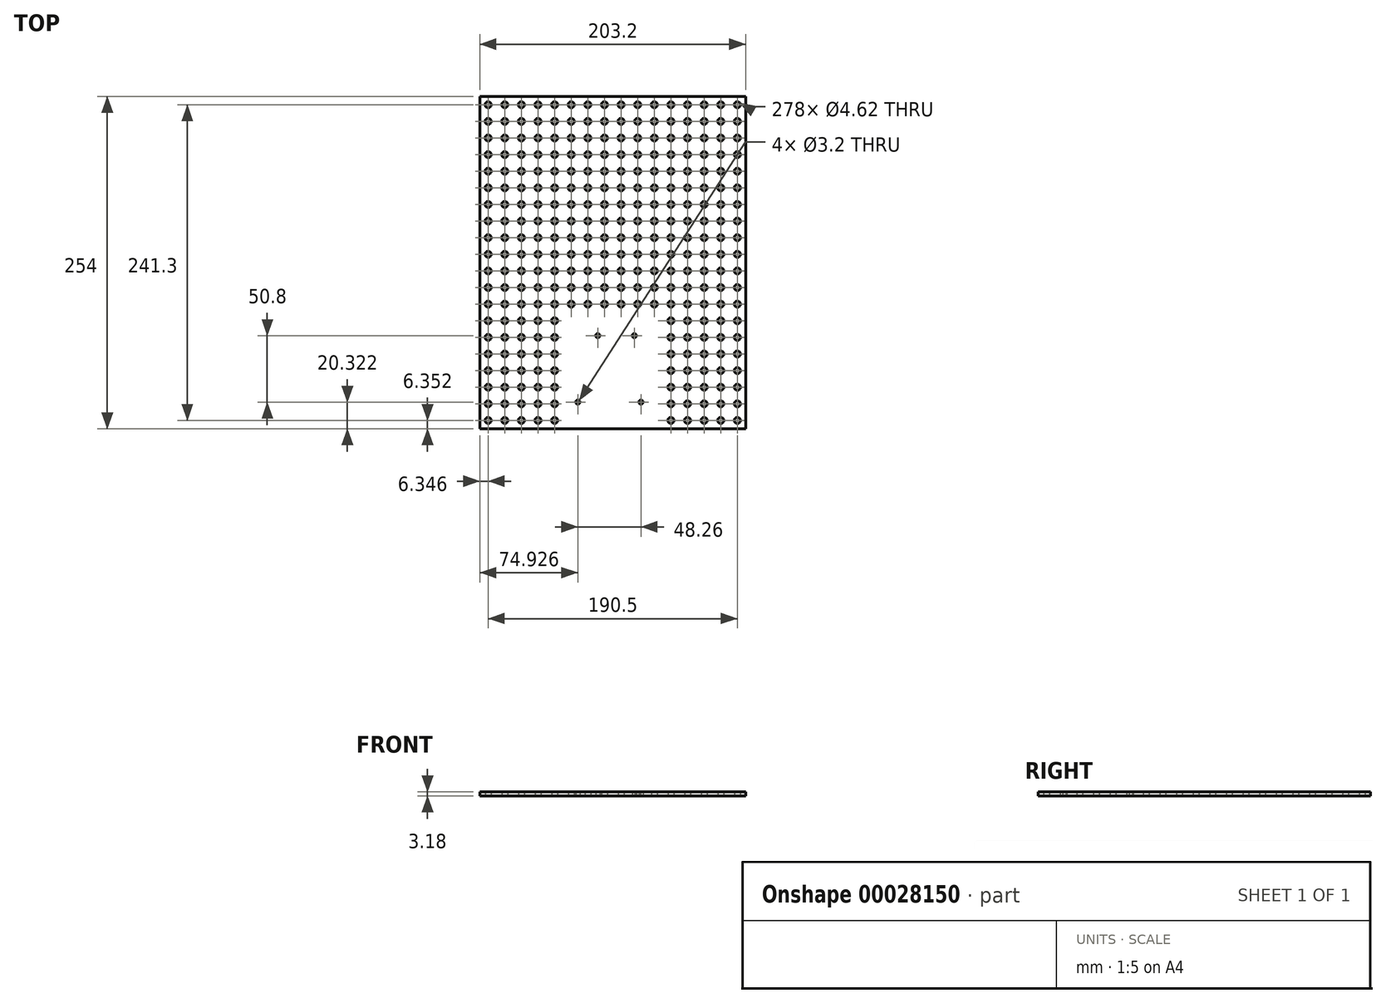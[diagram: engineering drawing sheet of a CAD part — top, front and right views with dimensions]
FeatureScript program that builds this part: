
annotation { "Feature Type Name" : "Feature", "Feature Type Description" : "" }
export const myFeature = defineFeature(function(context is Context, id is Id, definition is map)
    precondition{}
    {
        {
            var Q0;
            Q0=qCreatedBy(makeId("Top.planeOp"),FACE);
            var sketch = newSketch(context, id + "F0", { "sketchPlane" : qUnion([Q0])});
            skLineSegment(sketch, "E0.top", {"start": v(-127.4, -89.65) * mm, "end": v(-25.8, -89.65) * mm});
            skLineSegment(sketch, "E0.left", {"start": v(-127.4, 37.35) * mm, "end": v(-127.4, -89.65) * mm});
            skCircle(sketch, "E1", {"center": v(-121.04, 31) * mm, "radius": 2.31 * mm});
            skCircle(sketch, "E2", {"center": v(-121.04, 18.3) * mm, "radius": 2.31 * mm});
            skCircle(sketch, "E3", {"center": v(-121.04, 5.6) * mm, "radius": 2.31 * mm});
            skCircle(sketch, "E4", {"center": v(-121.04, -7.1) * mm, "radius": 2.31 * mm});
            skCircle(sketch, "E5", {"center": v(-121.04, -19.8) * mm, "radius": 2.31 * mm});
            skCircle(sketch, "E6", {"center": v(-121.04, -32.5) * mm, "radius": 2.31 * mm});
            skCircle(sketch, "E7", {"center": v(-121.04, -45.2) * mm, "radius": 2.31 * mm});
            skCircle(sketch, "E8", {"center": v(-121.04, -57.9) * mm, "radius": 2.31 * mm});
            skCircle(sketch, "E9", {"center": v(-121.04, -70.6) * mm, "radius": 2.31 * mm});
            skCircle(sketch, "E10", {"center": v(-121.04, -83.3) * mm, "radius": 2.31 * mm});
            skCircle(sketch, "E11.MirrorC", {"center": v(-108.34, 18.3) * mm, "radius": 2.31 * mm});
            skCircle(sketch, "E12.MirrorC", {"center": v(-108.34, -32.5) * mm, "radius": 2.31 * mm});
            skCircle(sketch, "E13.MirrorC", {"center": v(-108.34, -83.3) * mm, "radius": 2.31 * mm});
            skCircle(sketch, "E14.MirrorC", {"center": v(-108.34, -70.6) * mm, "radius": 2.31 * mm});
            skCircle(sketch, "E15.MirrorC", {"center": v(-108.34, 5.6) * mm, "radius": 2.31 * mm});
            skCircle(sketch, "E16.MirrorC", {"center": v(-108.34, -7.1) * mm, "radius": 2.31 * mm});
            skCircle(sketch, "E17.MirrorC", {"center": v(-108.34, -45.2) * mm, "radius": 2.31 * mm});
            skCircle(sketch, "E18.MirrorC", {"center": v(-108.34, -57.9) * mm, "radius": 2.31 * mm});
            skCircle(sketch, "E19.MirrorC", {"center": v(-108.34, -19.8) * mm, "radius": 2.31 * mm});
            skCircle(sketch, "E20.MirrorC", {"center": v(-108.34, 31) * mm, "radius": 2.31 * mm});
            skCircle(sketch, "E21.MirrorC", {"center": v(-95.64, -32.5) * mm, "radius": 2.31 * mm});
            skCircle(sketch, "E22.MirrorC", {"center": v(-82.94, -19.8) * mm, "radius": 2.31 * mm});
            skCircle(sketch, "E23.MirrorC", {"center": v(-95.64, 31) * mm, "radius": 2.31 * mm});
            skCircle(sketch, "E24.MirrorC", {"center": v(-95.64, -83.3) * mm, "radius": 2.31 * mm});
            skCircle(sketch, "E25.MirrorC", {"center": v(-82.94, -32.5) * mm, "radius": 2.31 * mm});
            skCircle(sketch, "E26.MirrorC", {"center": v(-95.64, 5.6) * mm, "radius": 2.31 * mm});
            skCircle(sketch, "E27.MirrorC", {"center": v(-95.64, -70.6) * mm, "radius": 2.31 * mm});
            skCircle(sketch, "E28.MirrorC", {"center": v(-82.94, -45.2) * mm, "radius": 2.31 * mm});
            skCircle(sketch, "E29.MirrorC", {"center": v(-95.64, -7.1) * mm, "radius": 2.31 * mm});
            skCircle(sketch, "E30.MirrorC", {"center": v(-82.94, -57.9) * mm, "radius": 2.31 * mm});
            skCircle(sketch, "E31.MirrorC", {"center": v(-95.64, -45.2) * mm, "radius": 2.31 * mm});
            skCircle(sketch, "E32.MirrorC", {"center": v(-95.64, -19.8) * mm, "radius": 2.31 * mm});
            skCircle(sketch, "E33.MirrorC", {"center": v(-82.94, 31) * mm, "radius": 2.31 * mm});
            skCircle(sketch, "E34.MirrorC", {"center": v(-82.94, 5.6) * mm, "radius": 2.31 * mm});
            skCircle(sketch, "E35.MirrorC", {"center": v(-95.64, 18.3) * mm, "radius": 2.31 * mm});
            skCircle(sketch, "E36.MirrorC", {"center": v(-82.94, -83.3) * mm, "radius": 2.31 * mm});
            skCircle(sketch, "E37.MirrorC", {"center": v(-95.64, -57.9) * mm, "radius": 2.31 * mm});
            skCircle(sketch, "E38.MirrorC", {"center": v(-82.94, 18.3) * mm, "radius": 2.31 * mm});
            skCircle(sketch, "E39.MirrorC", {"center": v(-82.94, -70.6) * mm, "radius": 2.31 * mm});
            skCircle(sketch, "E40.MirrorC", {"center": v(-82.94, -7.1) * mm, "radius": 2.31 * mm});
            skCircle(sketch, "E41.MirrorC", {"center": v(-70.24, -19.8) * mm, "radius": 2.31 * mm});
            skCircle(sketch, "E42.MirrorC", {"center": v(-70.24, -7.1) * mm, "radius": 2.31 * mm});
            skCircle(sketch, "E43.MirrorC", {"center": v(-44.84, 31) * mm, "radius": 2.31 * mm});
            skCircle(sketch, "E44.MirrorC", {"center": v(-70.24, 31) * mm, "radius": 2.31 * mm});
            skCircle(sketch, "E45.MirrorC", {"center": v(-57.54, 31) * mm, "radius": 2.31 * mm});
            skCircle(sketch, "E46.MirrorC", {"center": v(-44.84, 5.6) * mm, "radius": 2.31 * mm});
            skCircle(sketch, "E47.MirrorC", {"center": v(-70.24, -45.2) * mm, "radius": 2.31 * mm});
            skCircle(sketch, "E48.MirrorC", {"center": v(-70.24, 18.3) * mm, "radius": 2.31 * mm});
            skCircle(sketch, "E49.MirrorC", {"center": v(-70.24, 5.6) * mm, "radius": 2.31 * mm});
            skCircle(sketch, "E50.MirrorC", {"center": v(-70.24, -57.9) * mm, "radius": 2.31 * mm});
            skCircle(sketch, "E51.MirrorC", {"center": v(-57.54, 18.3) * mm, "radius": 2.31 * mm});
            skCircle(sketch, "E52.MirrorC", {"center": v(-32.14, 31) * mm, "radius": 2.31 * mm});
            skCircle(sketch, "E53.MirrorC", {"center": v(-70.24, -32.5) * mm, "radius": 2.31 * mm});
            skCircle(sketch, "E54.MirrorC", {"center": v(-32.14, 18.3) * mm, "radius": 2.31 * mm});
            skCircle(sketch, "E55.MirrorC", {"center": v(-44.84, 18.3) * mm, "radius": 2.31 * mm});
            skCircle(sketch, "E56.MirrorC", {"center": v(-57.54, 5.6) * mm, "radius": 2.31 * mm});
            skCircle(sketch, "E57.MirrorC", {"center": v(-70.24, -83.3) * mm, "radius": 2.31 * mm});
            skCircle(sketch, "E58.MirrorC", {"center": v(-32.14, 5.6) * mm, "radius": 2.31 * mm});
            skCircle(sketch, "E59.MirrorC", {"center": v(-70.24, -70.6) * mm, "radius": 2.31 * mm});
            skCircle(sketch, "E60.MirrorC", {"center": v(56.76, -7.1) * mm, "radius": 2.31 * mm});
            skCircle(sketch, "E61.MirrorC", {"center": v(44.06, -7.1) * mm, "radius": 2.31 * mm});
            skCircle(sketch, "E62.MirrorC", {"center": v(-19.44, 18.3) * mm, "radius": 2.31 * mm});
            skCircle(sketch, "E63.MirrorC", {"center": v(56.76, -83.3) * mm, "radius": 2.31 * mm});
            skCircle(sketch, "E64.MirrorC", {"center": v(44.06, 18.3) * mm, "radius": 2.31 * mm});
            skCircle(sketch, "E65.MirrorC", {"center": v(56.76, 5.6) * mm, "radius": 2.31 * mm});
            skCircle(sketch, "E66.MirrorC", {"center": v(56.76, 18.3) * mm, "radius": 2.31 * mm});
            skCircle(sketch, "E67.MirrorC", {"center": v(-19.44, 5.6) * mm, "radius": 2.31 * mm});
            skCircle(sketch, "E68.MirrorC", {"center": v(44.06, 5.6) * mm, "radius": 2.31 * mm});
            skCircle(sketch, "E69.MirrorC", {"center": v(18.66, -7.1) * mm, "radius": 2.31 * mm});
            skCircle(sketch, "E70.MirrorC", {"center": v(31.36, -19.8) * mm, "radius": 2.31 * mm});
            skCircle(sketch, "E71.MirrorC", {"center": v(69.46, -7.1) * mm, "radius": 2.31 * mm});
            skCircle(sketch, "E72.MirrorC", {"center": v(44.06, -32.5) * mm, "radius": 2.31 * mm});
            skCircle(sketch, "E73.MirrorC", {"center": v(44.06, -19.8) * mm, "radius": 2.31 * mm});
            skCircle(sketch, "E74.MirrorC", {"center": v(31.36, -70.6) * mm, "radius": 2.31 * mm});
            skCircle(sketch, "E75.MirrorC", {"center": v(69.46, 5.6) * mm, "radius": 2.31 * mm});
            skCircle(sketch, "E76.MirrorC", {"center": v(5.96, 5.6) * mm, "radius": 2.31 * mm});
            skCircle(sketch, "E77.MirrorC", {"center": v(56.76, -57.9) * mm, "radius": 2.31 * mm});
            skCircle(sketch, "E78.MirrorC", {"center": v(44.06, -45.2) * mm, "radius": 2.31 * mm});
            skCircle(sketch, "E79.MirrorC", {"center": v(69.46, 18.3) * mm, "radius": 2.31 * mm});
            skCircle(sketch, "E80.MirrorC", {"center": v(18.66, -45.2) * mm, "radius": 2.31 * mm});
            skCircle(sketch, "E81.MirrorC", {"center": v(5.96, 18.3) * mm, "radius": 2.31 * mm});
            skLineSegment(sketch, "E82.MirrorCS", {"start": v(75.8, 37.35) * mm, "end": v(75.8, -89.65) * mm});
            skLineSegment(sketch, "E83.MirrorCS", {"start": v(75.8, -89.65) * mm, "end": v(-25.8, -89.65) * mm});
            skCircle(sketch, "E84.MirrorC", {"center": v(69.46, 31) * mm, "radius": 2.31 * mm});
            skCircle(sketch, "E85.MirrorC", {"center": v(18.66, -19.8) * mm, "radius": 2.31 * mm});
            skCircle(sketch, "E86.MirrorC", {"center": v(-6.74, 5.6) * mm, "radius": 2.31 * mm});
            skCircle(sketch, "E87.MirrorC", {"center": v(18.66, -57.9) * mm, "radius": 2.31 * mm});
            skCircle(sketch, "E88.MirrorC", {"center": v(56.76, -45.2) * mm, "radius": 2.31 * mm});
            skCircle(sketch, "E89.MirrorC", {"center": v(31.36, -57.9) * mm, "radius": 2.31 * mm});
            skCircle(sketch, "E90.MirrorC", {"center": v(-6.74, 18.3) * mm, "radius": 2.31 * mm});
            skCircle(sketch, "E91.MirrorC", {"center": v(5.96, 31) * mm, "radius": 2.31 * mm});
            skCircle(sketch, "E92.MirrorC", {"center": v(31.36, 18.3) * mm, "radius": 2.31 * mm});
            skCircle(sketch, "E93.MirrorC", {"center": v(56.76, -70.6) * mm, "radius": 2.31 * mm});
            skCircle(sketch, "E94.MirrorC", {"center": v(31.36, -45.2) * mm, "radius": 2.31 * mm});
            skCircle(sketch, "E95.MirrorC", {"center": v(44.06, -57.9) * mm, "radius": 2.31 * mm});
            skCircle(sketch, "E96.MirrorC", {"center": v(18.66, 31) * mm, "radius": 2.31 * mm});
            skCircle(sketch, "E97.MirrorC", {"center": v(56.76, 31) * mm, "radius": 2.31 * mm});
            skCircle(sketch, "E98.MirrorC", {"center": v(44.06, -70.6) * mm, "radius": 2.31 * mm});
            skCircle(sketch, "E99.MirrorC", {"center": v(18.66, 18.3) * mm, "radius": 2.31 * mm});
            skCircle(sketch, "E100.MirrorC", {"center": v(69.46, -70.6) * mm, "radius": 2.31 * mm});
            skCircle(sketch, "E101.MirrorC", {"center": v(18.66, -70.6) * mm, "radius": 2.31 * mm});
            skCircle(sketch, "E102.MirrorC", {"center": v(56.76, -19.8) * mm, "radius": 2.31 * mm});
            skCircle(sketch, "E103.MirrorC", {"center": v(56.76, -32.5) * mm, "radius": 2.31 * mm});
            skCircle(sketch, "E104.MirrorC", {"center": v(31.36, -32.5) * mm, "radius": 2.31 * mm});
            skCircle(sketch, "E105.MirrorC", {"center": v(69.46, -57.9) * mm, "radius": 2.31 * mm});
            skCircle(sketch, "E106.MirrorC", {"center": v(-19.44, 31) * mm, "radius": 2.31 * mm});
            skCircle(sketch, "E107.MirrorC", {"center": v(18.66, -32.5) * mm, "radius": 2.31 * mm});
            skCircle(sketch, "E108.MirrorC", {"center": v(44.06, -83.3) * mm, "radius": 2.31 * mm});
            skCircle(sketch, "E109.MirrorC", {"center": v(31.36, 5.6) * mm, "radius": 2.31 * mm});
            skCircle(sketch, "E110.MirrorC", {"center": v(69.46, -45.2) * mm, "radius": 2.31 * mm});
            skCircle(sketch, "E111.MirrorC", {"center": v(-6.74, 31) * mm, "radius": 2.31 * mm});
            skCircle(sketch, "E112.MirrorC", {"center": v(18.66, -83.3) * mm, "radius": 2.31 * mm});
            skCircle(sketch, "E113.MirrorC", {"center": v(44.06, 31) * mm, "radius": 2.31 * mm});
            skCircle(sketch, "E114.MirrorC", {"center": v(31.36, 31) * mm, "radius": 2.31 * mm});
            skCircle(sketch, "E115.MirrorC", {"center": v(69.46, -32.5) * mm, "radius": 2.31 * mm});
            skCircle(sketch, "E116.MirrorC", {"center": v(18.66, 5.6) * mm, "radius": 2.31 * mm});
            skCircle(sketch, "E117.MirrorC", {"center": v(69.46, -83.3) * mm, "radius": 2.31 * mm});
            skCircle(sketch, "E118.MirrorC", {"center": v(69.46, -19.8) * mm, "radius": 2.31 * mm});
            skCircle(sketch, "E119.MirrorC", {"center": v(31.36, -83.3) * mm, "radius": 2.31 * mm});
            skCircle(sketch, "E120.MirrorC", {"center": v(31.36, -7.1) * mm, "radius": 2.31 * mm});
            skCircle(sketch, "E121.MirrorC", {"center": v(-44.84, 132.6) * mm, "radius": 2.31 * mm});
            skCircle(sketch, "E122.MirrorC", {"center": v(-95.64, 158) * mm, "radius": 2.31 * mm});
            skCircle(sketch, "E123.MirrorC", {"center": v(-95.64, 69.1) * mm, "radius": 2.31 * mm});
            skCircle(sketch, "E124.MirrorC", {"center": v(-82.94, 132.6) * mm, "radius": 2.31 * mm});
            skCircle(sketch, "E125.MirrorC", {"center": v(-121.04, 119.9) * mm, "radius": 2.31 * mm});
            skCircle(sketch, "E126.MirrorC", {"center": v(-19.44, 119.9) * mm, "radius": 2.31 * mm});
            skCircle(sketch, "E127.MirrorC", {"center": v(-82.94, 81.8) * mm, "radius": 2.31 * mm});
            skCircle(sketch, "E128.MirrorC", {"center": v(-70.24, 81.8) * mm, "radius": 2.31 * mm});
            skCircle(sketch, "E129.MirrorC", {"center": v(-121.04, 107.2) * mm, "radius": 2.31 * mm});
            skCircle(sketch, "E130.MirrorC", {"center": v(-32.14, 43.7) * mm, "radius": 2.31 * mm});
            skCircle(sketch, "E131.MirrorC", {"center": v(-70.24, 43.7) * mm, "radius": 2.31 * mm});
            skCircle(sketch, "E132.MirrorC", {"center": v(-95.64, 94.5) * mm, "radius": 2.31 * mm});
            skCircle(sketch, "E133.MirrorC", {"center": v(18.66, 107.2) * mm, "radius": 2.31 * mm});
            skCircle(sketch, "E134.MirrorC", {"center": v(56.76, 43.7) * mm, "radius": 2.31 * mm});
            skCircle(sketch, "E135.MirrorC", {"center": v(18.66, 94.5) * mm, "radius": 2.31 * mm});
            skCircle(sketch, "E136.MirrorC", {"center": v(31.36, 94.5) * mm, "radius": 2.31 * mm});
            skCircle(sketch, "E137.MirrorC", {"center": v(18.66, 43.7) * mm, "radius": 2.31 * mm});
            skCircle(sketch, "E138.MirrorC", {"center": v(18.66, 81.8) * mm, "radius": 2.31 * mm});
            skCircle(sketch, "E139.MirrorC", {"center": v(-6.74, 119.9) * mm, "radius": 2.31 * mm});
            skCircle(sketch, "E140.MirrorC", {"center": v(-57.54, 81.8) * mm, "radius": 2.31 * mm});
            skCircle(sketch, "E141.MirrorC", {"center": v(31.36, 158) * mm, "radius": 2.31 * mm});
            skCircle(sketch, "E142.MirrorC", {"center": v(-121.04, 94.5) * mm, "radius": 2.31 * mm});
            skCircle(sketch, "E143.MirrorC", {"center": v(-121.04, 69.1) * mm, "radius": 2.31 * mm});
            skCircle(sketch, "E144.MirrorC", {"center": v(-44.84, 56.4) * mm, "radius": 2.31 * mm});
            skCircle(sketch, "E145.MirrorC", {"center": v(69.46, 69.1) * mm, "radius": 2.31 * mm});
            skCircle(sketch, "E146.MirrorC", {"center": v(5.96, 43.7) * mm, "radius": 2.31 * mm});
            skCircle(sketch, "E147.MirrorC", {"center": v(69.46, 81.8) * mm, "radius": 2.31 * mm});
            skCircle(sketch, "E148.MirrorC", {"center": v(-6.74, 69.1) * mm, "radius": 2.31 * mm});
            skCircle(sketch, "E149.MirrorC", {"center": v(-82.94, 56.4) * mm, "radius": 2.31 * mm});
            skCircle(sketch, "E150.MirrorC", {"center": v(-70.24, 56.4) * mm, "radius": 2.31 * mm});
            skCircle(sketch, "E151.MirrorC", {"center": v(-121.04, 43.7) * mm, "radius": 2.31 * mm});
            skCircle(sketch, "E152.MirrorC", {"center": v(-121.04, 81.8) * mm, "radius": 2.31 * mm});
            skCircle(sketch, "E153.MirrorC", {"center": v(-108.34, 119.9) * mm, "radius": 2.31 * mm});
            skCircle(sketch, "E154.MirrorC", {"center": v(31.36, 145.3) * mm, "radius": 2.31 * mm});
            skCircle(sketch, "E155.MirrorC", {"center": v(-19.44, 158) * mm, "radius": 2.31 * mm});
            skCircle(sketch, "E156.MirrorC", {"center": v(-44.84, 107.2) * mm, "radius": 2.31 * mm});
            skCircle(sketch, "E157.MirrorC", {"center": v(-57.54, 43.7) * mm, "radius": 2.31 * mm});
            skCircle(sketch, "E158.MirrorC", {"center": v(-82.94, 43.7) * mm, "radius": 2.31 * mm});
            skCircle(sketch, "E159.MirrorC", {"center": v(-108.34, 145.3) * mm, "radius": 2.31 * mm});
            skCircle(sketch, "E160.MirrorC", {"center": v(5.96, 119.9) * mm, "radius": 2.31 * mm});
            skCircle(sketch, "E161.MirrorC", {"center": v(-108.34, 158) * mm, "radius": 2.31 * mm});
            skCircle(sketch, "E162.MirrorC", {"center": v(-108.34, 107.2) * mm, "radius": 2.31 * mm});
            skCircle(sketch, "E163.MirrorC", {"center": v(18.66, 56.4) * mm, "radius": 2.31 * mm});
            skCircle(sketch, "E164.MirrorC", {"center": v(-19.44, 43.7) * mm, "radius": 2.31 * mm});
            skCircle(sketch, "E165.MirrorC", {"center": v(-6.74, 81.8) * mm, "radius": 2.31 * mm});
            skCircle(sketch, "E166.MirrorC", {"center": v(31.36, 107.2) * mm, "radius": 2.31 * mm});
            skCircle(sketch, "E167.MirrorC", {"center": v(-19.44, 94.5) * mm, "radius": 2.31 * mm});
            skCircle(sketch, "E168.MirrorC", {"center": v(-57.54, 107.2) * mm, "radius": 2.31 * mm});
            skCircle(sketch, "E169.MirrorC", {"center": v(56.76, 56.4) * mm, "radius": 2.31 * mm});
            skCircle(sketch, "E170.MirrorC", {"center": v(18.66, 119.9) * mm, "radius": 2.31 * mm});
            skCircle(sketch, "E171.MirrorC", {"center": v(-19.44, 132.6) * mm, "radius": 2.31 * mm});
            skCircle(sketch, "E172.MirrorC", {"center": v(-19.44, 56.4) * mm, "radius": 2.31 * mm});
            skCircle(sketch, "E173.MirrorC", {"center": v(44.06, 145.3) * mm, "radius": 2.31 * mm});
            skCircle(sketch, "E174.MirrorC", {"center": v(-95.64, 145.3) * mm, "radius": 2.31 * mm});
            skCircle(sketch, "E175.MirrorC", {"center": v(-57.54, 145.3) * mm, "radius": 2.31 * mm});
            skCircle(sketch, "E176.MirrorC", {"center": v(69.46, 43.7) * mm, "radius": 2.31 * mm});
            skCircle(sketch, "E177.MirrorC", {"center": v(-6.74, 56.4) * mm, "radius": 2.31 * mm});
            skCircle(sketch, "E178.MirrorC", {"center": v(-6.74, 145.3) * mm, "radius": 2.31 * mm});
            skCircle(sketch, "E179.MirrorC", {"center": v(-32.14, 132.6) * mm, "radius": 2.31 * mm});
            skCircle(sketch, "E180.MirrorC", {"center": v(44.06, 119.9) * mm, "radius": 2.31 * mm});
            skCircle(sketch, "E181.MirrorC", {"center": v(-121.04, 56.4) * mm, "radius": 2.31 * mm});
            skCircle(sketch, "E182.MirrorC", {"center": v(56.76, 119.9) * mm, "radius": 2.31 * mm});
            skCircle(sketch, "E183.MirrorC", {"center": v(5.96, 145.3) * mm, "radius": 2.31 * mm});
            skCircle(sketch, "E184.MirrorC", {"center": v(5.96, 81.8) * mm, "radius": 2.31 * mm});
            skCircle(sketch, "E185.MirrorC", {"center": v(44.06, 158) * mm, "radius": 2.31 * mm});
            skCircle(sketch, "E186.MirrorC", {"center": v(-32.14, 107.2) * mm, "radius": 2.31 * mm});
            skCircle(sketch, "E187.MirrorC", {"center": v(-44.84, 94.5) * mm, "radius": 2.31 * mm});
            skCircle(sketch, "E188.MirrorC", {"center": v(-70.24, 145.3) * mm, "radius": 2.31 * mm});
            skCircle(sketch, "E189.MirrorC", {"center": v(-70.24, 158) * mm, "radius": 2.31 * mm});
            skCircle(sketch, "E190.MirrorC", {"center": v(56.76, 69.1) * mm, "radius": 2.31 * mm});
            skCircle(sketch, "E191.MirrorC", {"center": v(69.46, 56.4) * mm, "radius": 2.31 * mm});
            skCircle(sketch, "E192.MirrorC", {"center": v(-44.84, 81.8) * mm, "radius": 2.31 * mm});
            skCircle(sketch, "E193.MirrorC", {"center": v(69.46, 158) * mm, "radius": 2.31 * mm});
            skCircle(sketch, "E194.MirrorC", {"center": v(44.06, 69.1) * mm, "radius": 2.31 * mm});
            skCircle(sketch, "E195.MirrorC", {"center": v(44.06, 132.6) * mm, "radius": 2.31 * mm});
            skCircle(sketch, "E196.MirrorC", {"center": v(5.96, 107.2) * mm, "radius": 2.31 * mm});
            skCircle(sketch, "E197.MirrorC", {"center": v(-95.64, 81.8) * mm, "radius": 2.31 * mm});
            skCircle(sketch, "E198.MirrorC", {"center": v(-44.84, 158) * mm, "radius": 2.31 * mm});
            skCircle(sketch, "E199.MirrorC", {"center": v(-57.54, 56.4) * mm, "radius": 2.31 * mm});
            skCircle(sketch, "E200.MirrorC", {"center": v(-32.14, 94.5) * mm, "radius": 2.31 * mm});
            skCircle(sketch, "E201.MirrorC", {"center": v(5.96, 158) * mm, "radius": 2.31 * mm});
            skCircle(sketch, "E202.MirrorC", {"center": v(18.66, 145.3) * mm, "radius": 2.31 * mm});
            skCircle(sketch, "E203.MirrorC", {"center": v(69.46, 107.2) * mm, "radius": 2.31 * mm});
            skCircle(sketch, "E204.MirrorC", {"center": v(-32.14, 158) * mm, "radius": 2.31 * mm});
            skCircle(sketch, "E205.MirrorC", {"center": v(-6.74, 158) * mm, "radius": 2.31 * mm});
            skCircle(sketch, "E206.MirrorC", {"center": v(56.76, 145.3) * mm, "radius": 2.31 * mm});
            skCircle(sketch, "E207.MirrorC", {"center": v(-82.94, 107.2) * mm, "radius": 2.31 * mm});
            skCircle(sketch, "E208.MirrorC", {"center": v(-108.34, 94.5) * mm, "radius": 2.31 * mm});
            skCircle(sketch, "E209.MirrorC", {"center": v(-19.44, 81.8) * mm, "radius": 2.31 * mm});
            skCircle(sketch, "E210.MirrorC", {"center": v(-6.74, 43.7) * mm, "radius": 2.31 * mm});
            skCircle(sketch, "E211.MirrorC", {"center": v(-70.24, 107.2) * mm, "radius": 2.31 * mm});
            skCircle(sketch, "E212.MirrorC", {"center": v(-70.24, 119.9) * mm, "radius": 2.31 * mm});
            skCircle(sketch, "E213.MirrorC", {"center": v(-95.64, 56.4) * mm, "radius": 2.31 * mm});
            skCircle(sketch, "E214.MirrorC", {"center": v(44.06, 107.2) * mm, "radius": 2.31 * mm});
            skCircle(sketch, "E215.MirrorC", {"center": v(-108.34, 69.1) * mm, "radius": 2.31 * mm});
            skCircle(sketch, "E216.MirrorC", {"center": v(-57.54, 94.5) * mm, "radius": 2.31 * mm});
            skCircle(sketch, "E217.MirrorC", {"center": v(-44.84, 119.9) * mm, "radius": 2.31 * mm});
            skCircle(sketch, "E218.MirrorC", {"center": v(-95.64, 132.6) * mm, "radius": 2.31 * mm});
            skCircle(sketch, "E219.MirrorC", {"center": v(-57.54, 132.6) * mm, "radius": 2.31 * mm});
            skCircle(sketch, "E220.MirrorC", {"center": v(-95.64, 119.9) * mm, "radius": 2.31 * mm});
            skCircle(sketch, "E221.MirrorC", {"center": v(-108.34, 43.7) * mm, "radius": 2.31 * mm});
            skCircle(sketch, "E222.MirrorC", {"center": v(56.76, 81.8) * mm, "radius": 2.31 * mm});
            skCircle(sketch, "E223.MirrorC", {"center": v(-57.54, 119.9) * mm, "radius": 2.31 * mm});
            skCircle(sketch, "E224.MirrorC", {"center": v(-44.84, 145.3) * mm, "radius": 2.31 * mm});
            skCircle(sketch, "E225.MirrorC", {"center": v(69.46, 119.9) * mm, "radius": 2.31 * mm});
            skCircle(sketch, "E226.MirrorC", {"center": v(-82.94, 158) * mm, "radius": 2.31 * mm});
            skCircle(sketch, "E227.MirrorC", {"center": v(69.46, 145.3) * mm, "radius": 2.31 * mm});
            skCircle(sketch, "E228.MirrorC", {"center": v(31.36, 132.6) * mm, "radius": 2.31 * mm});
            skCircle(sketch, "E229.MirrorC", {"center": v(44.06, 94.5) * mm, "radius": 2.31 * mm});
            skCircle(sketch, "E230.MirrorC", {"center": v(-32.14, 119.9) * mm, "radius": 2.31 * mm});
            skCircle(sketch, "E231.MirrorC", {"center": v(-82.94, 94.5) * mm, "radius": 2.31 * mm});
            skCircle(sketch, "E232.MirrorC", {"center": v(56.76, 107.2) * mm, "radius": 2.31 * mm});
            skCircle(sketch, "E233.MirrorC", {"center": v(-32.14, 56.4) * mm, "radius": 2.31 * mm});
            skCircle(sketch, "E234.MirrorC", {"center": v(44.06, 81.8) * mm, "radius": 2.31 * mm});
            skCircle(sketch, "E235.MirrorC", {"center": v(-95.64, 107.2) * mm, "radius": 2.31 * mm});
            skCircle(sketch, "E236.MirrorC", {"center": v(-6.74, 107.2) * mm, "radius": 2.31 * mm});
            skCircle(sketch, "E237.MirrorC", {"center": v(44.06, 43.7) * mm, "radius": 2.31 * mm});
            skCircle(sketch, "E238.MirrorC", {"center": v(31.36, 81.8) * mm, "radius": 2.31 * mm});
            skCircle(sketch, "E239.MirrorC", {"center": v(-32.14, 81.8) * mm, "radius": 2.31 * mm});
            skCircle(sketch, "E240.MirrorC", {"center": v(56.76, 158) * mm, "radius": 2.31 * mm});
            skCircle(sketch, "E241.MirrorC", {"center": v(5.96, 69.1) * mm, "radius": 2.31 * mm});
            skCircle(sketch, "E242.MirrorC", {"center": v(-19.44, 145.3) * mm, "radius": 2.31 * mm});
            skCircle(sketch, "E243.MirrorC", {"center": v(31.36, 56.4) * mm, "radius": 2.31 * mm});
            skCircle(sketch, "E244.MirrorC", {"center": v(-95.64, 43.7) * mm, "radius": 2.31 * mm});
            skCircle(sketch, "E245.MirrorC", {"center": v(-82.94, 145.3) * mm, "radius": 2.31 * mm});
            skCircle(sketch, "E246.MirrorC", {"center": v(18.66, 69.1) * mm, "radius": 2.31 * mm});
            skCircle(sketch, "E247.MirrorC", {"center": v(-19.44, 69.1) * mm, "radius": 2.31 * mm});
            skCircle(sketch, "E248.MirrorC", {"center": v(5.96, 56.4) * mm, "radius": 2.31 * mm});
            skCircle(sketch, "E249.MirrorC", {"center": v(31.36, 119.9) * mm, "radius": 2.31 * mm});
            skCircle(sketch, "E250.MirrorC", {"center": v(18.66, 132.6) * mm, "radius": 2.31 * mm});
            skCircle(sketch, "E251.MirrorC", {"center": v(5.96, 132.6) * mm, "radius": 2.31 * mm});
            skCircle(sketch, "E252.MirrorC", {"center": v(69.46, 94.5) * mm, "radius": 2.31 * mm});
            skCircle(sketch, "E253.MirrorC", {"center": v(31.36, 69.1) * mm, "radius": 2.31 * mm});
            skCircle(sketch, "E254.MirrorC", {"center": v(-82.94, 69.1) * mm, "radius": 2.31 * mm});
            skCircle(sketch, "E255.MirrorC", {"center": v(-44.84, 69.1) * mm, "radius": 2.31 * mm});
            skCircle(sketch, "E256.MirrorC", {"center": v(-32.14, 145.3) * mm, "radius": 2.31 * mm});
            skCircle(sketch, "E257.MirrorC", {"center": v(-6.74, 94.5) * mm, "radius": 2.31 * mm});
            skCircle(sketch, "E258.MirrorC", {"center": v(-70.24, 69.1) * mm, "radius": 2.31 * mm});
            skCircle(sketch, "E259.MirrorC", {"center": v(-19.44, 107.2) * mm, "radius": 2.31 * mm});
            skCircle(sketch, "E260.MirrorC", {"center": v(18.66, 158) * mm, "radius": 2.31 * mm});
            skCircle(sketch, "E261.MirrorC", {"center": v(-108.34, 132.6) * mm, "radius": 2.31 * mm});
            skCircle(sketch, "E262.MirrorC", {"center": v(5.96, 94.5) * mm, "radius": 2.31 * mm});
            skCircle(sketch, "E263.MirrorC", {"center": v(69.46, 132.6) * mm, "radius": 2.31 * mm});
            skCircle(sketch, "E264.MirrorC", {"center": v(-82.94, 119.9) * mm, "radius": 2.31 * mm});
            skCircle(sketch, "E265.MirrorC", {"center": v(-44.84, 43.7) * mm, "radius": 2.31 * mm});
            skCircle(sketch, "E266.MirrorC", {"center": v(56.76, 94.5) * mm, "radius": 2.31 * mm});
            skCircle(sketch, "E267.MirrorC", {"center": v(-70.24, 132.6) * mm, "radius": 2.31 * mm});
            skCircle(sketch, "E268.MirrorC", {"center": v(-32.14, 69.1) * mm, "radius": 2.31 * mm});
            skCircle(sketch, "E269.MirrorC", {"center": v(31.36, 43.7) * mm, "radius": 2.31 * mm});
            skCircle(sketch, "E270.MirrorC", {"center": v(-57.54, 69.1) * mm, "radius": 2.31 * mm});
            skCircle(sketch, "E271.MirrorC", {"center": v(-70.24, 94.5) * mm, "radius": 2.31 * mm});
            skCircle(sketch, "E272.MirrorC", {"center": v(44.06, 56.4) * mm, "radius": 2.31 * mm});
            skCircle(sketch, "E273.MirrorC", {"center": v(-108.34, 56.4) * mm, "radius": 2.31 * mm});
            skCircle(sketch, "E274.MirrorC", {"center": v(-121.04, 158) * mm, "radius": 2.31 * mm});
            skCircle(sketch, "E275.MirrorC", {"center": v(56.76, 132.6) * mm, "radius": 2.31 * mm});
            skCircle(sketch, "E276.MirrorC", {"center": v(-108.34, 81.8) * mm, "radius": 2.31 * mm});
            skCircle(sketch, "E277.MirrorC", {"center": v(-57.54, 158) * mm, "radius": 2.31 * mm});
            skCircle(sketch, "E278.MirrorC", {"center": v(-6.74, 132.6) * mm, "radius": 2.31 * mm});
            skCircle(sketch, "E279.MirrorC", {"center": v(-121.04, 145.3) * mm, "radius": 2.31 * mm});
            skCircle(sketch, "E280.MirrorC", {"center": v(-121.04, 132.6) * mm, "radius": 2.31 * mm});
            skLineSegment(sketch, "E281.MirrorCS", {"start": v(75.8, 164.35) * mm, "end": v(-25.8, 164.35) * mm});
            skLineSegment(sketch, "E282.MirrorCS", {"start": v(-127.4, 37.35) * mm, "end": v(-127.4, 164.35) * mm});
            skLineSegment(sketch, "E283.MirrorCS", {"start": v(-127.4, 164.35) * mm, "end": v(-25.8, 164.35) * mm});
            skLineSegment(sketch, "E284.MirrorCS", {"start": v(75.8, 37.35) * mm, "end": v(75.8, 164.35) * mm});
            skLineSegment(sketch, "E285", {"start": v(-57.54, -83.3) * mm, "end": v(5.96, -83.3) * mm, "construction": true});
            skLineSegment(sketch, "E286", {"start": v(-57.54, -7.1) * mm, "end": v(5.96, -7.1) * mm, "construction": true});
            skLineSegment(sketch, "E287", {"start": v(-57.54, -83.3) * mm, "end": v(-57.54, -7.1) * mm, "construction": true});
            skLineSegment(sketch, "E288", {"start": v(5.96, -7.1) * mm, "end": v(5.96, -83.3) * mm, "construction": true});
            skPoint(sketch, "E289", {"position": v(-52.46, -69.33) * mm});
            skCircle(sketch, "E290", {"center": v(-52.46, -69.33) * mm, "radius": 1.6 * mm});
            skCircle(sketch, "E291", {"center": v(-37.22, -18.53) * mm, "radius": 1.6 * mm});
            skCircle(sketch, "E292", {"center": v(-9.28, -18.53) * mm, "radius": 1.6 * mm});
            skCircle(sketch, "E293", {"center": v(-4.2, -69.33) * mm, "radius": 1.6 * mm});
            skSolve(sketch);
        }
        {
            var Q0;
            Q0=makeQuery(id+"F0.imprint","IMPRINT",FACE,{"disambiguationData":[TD([[makeQuery(id+"F0.imprint","IMPRINT",EDGE,{"derivedFrom":sQuery(id+"F0.wireOp",EDGE,"E0.top")}),1.0]])]});
            extrude(context, id + "F1", {"entities" : qUnion([Q0]), "depth" : 3.17 * mm});
        }
    });
